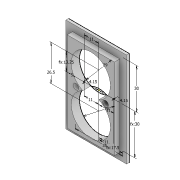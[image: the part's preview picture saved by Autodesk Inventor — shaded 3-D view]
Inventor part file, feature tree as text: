
AUTODESK INVENTOR PART (.ipt)
format: ipt  version: 2022 (Build 260153000, 153)  size: 117,248 bytes
history: native  units: mm
features: extrude x2, sketch x1
ambient origin geometry x8: Origin, YZ Plane, XZ Plane, XY Plane, X Axis, Y Axis, Z Axis, Center Point
bodies: Solid1 (feature_tree)
feature tree (3):
  sketch  "Sketch1"  dims[d0=29.0mm d1=29.0mm d2=26.5mm d3=13.25mm d6=0.0mm d7=4.15mm d8=4.15mm d9=11.0mm d10=11.0mm d11=11.0mm d12=11.0mm d13=35.0mm d14=17.5mm d15=30.0mm d16=30.0mm d17=5.0mm d18=2.0mm d19=0.0mm d20=6.0mm d21=0.0mm]
  extrude  "Extrusion1"  Depth=6.0mm
  extrude  "Extrusion2"  Depth=6.0mm
